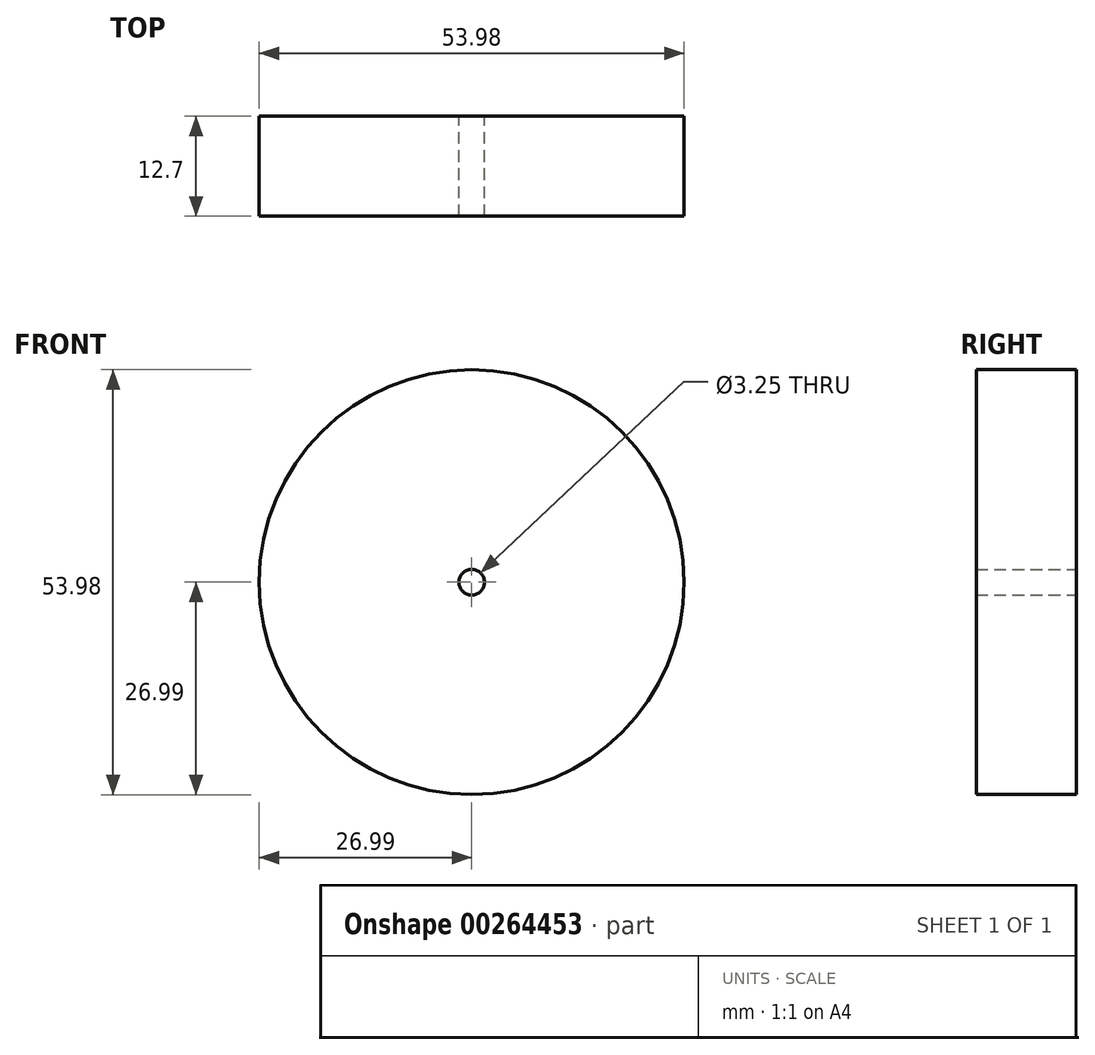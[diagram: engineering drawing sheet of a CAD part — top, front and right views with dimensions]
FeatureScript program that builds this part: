
annotation { "Feature Type Name" : "Feature", "Feature Type Description" : "" }
export const myFeature = defineFeature(function(context is Context, id is Id, definition is map)
    precondition{}
    {
        {
            var Q0;
            Q0=qCreatedBy(makeId("Front.planeOp"),FACE);
            var sketch = newSketch(context, id + "F0", { "sketchPlane" : qUnion([Q0])});
            skCircle(sketch, "E0", {"center": v(0, 0) * mm, "radius": 1.63 * mm});
            skCircle(sketch, "E1", {"center": v(0, 0) * mm, "radius": 26.99 * mm});
            skSolve(sketch);
        }
        {
            var Q0;
            Q0=makeQuery(id+"F0.imprint","IMPRINT",FACE,{"disambiguationData":[TD([[makeQuery(id+"F0.imprint","IMPRINT",EDGE,{"derivedFrom":sQuery(id+"F0.wireOp",EDGE,"GwJEcJbn-paQn-5j7e-cp30-MJ4dQJ4qUo2g")}),1.0]])]});
            var Q1;
            Q1=makeQuery(id+"F0.imprint","IMPRINT",FACE,{"disambiguationData":[TD([[makeQuery(id+"F0.imprint","IMPRINT",EDGE,{"derivedFrom":sQuery(id+"F0.wireOp",EDGE,"E0")}),-1.0]])]});
            extrude(context, id + "F1", {"entities" : qUnion([Q0, Q1]), "depth" : 12.7 * mm});
        }
    });
